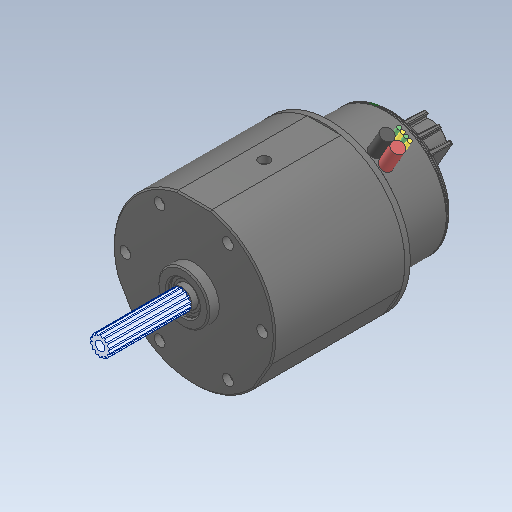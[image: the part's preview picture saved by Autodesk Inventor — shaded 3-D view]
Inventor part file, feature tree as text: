
AUTODESK INVENTOR PART (.ipt)
format: ipt  version: 2020 (Build 240168000, 168)  size: 1,356,800 bytes
history: native  units: in
note: dims shown in document units (in); Inventor stores cm internally (conversion verified against a paired STEP export)
features: fillet x4, other x2, chamfer x1
ambient origin geometry x8: Origin, YZ Plane, XZ Plane, XY Plane, X Axis, Y Axis, Z Axis, Center Point
bodies: Solid1 (feature_tree), Solid2 (feature_tree), Solid3 (feature_tree), Solid4 (feature_tree), Solid5 (feature_tree), Solid6 (feature_tree), Solid7 (feature_tree)
feature tree (7):
  chamfer  "Chamfer3"  [1 undecoded]
  other  "Boss-Extrude10"
  fillet  "Fillet4"  [1 undecoded]
  fillet  "Fillet3"  [1 undecoded]
  fillet  "Fillet5"  [1 undecoded]
  fillet  "Fillet6"  [1 undecoded]
  other  "#8-32 Tapped Hole1"
note: 5 required parameter values undecoded (feature->parameter linkage not recoverable at this tier; creation-order binding heuristic only, values carry confidence <= 0.55)
